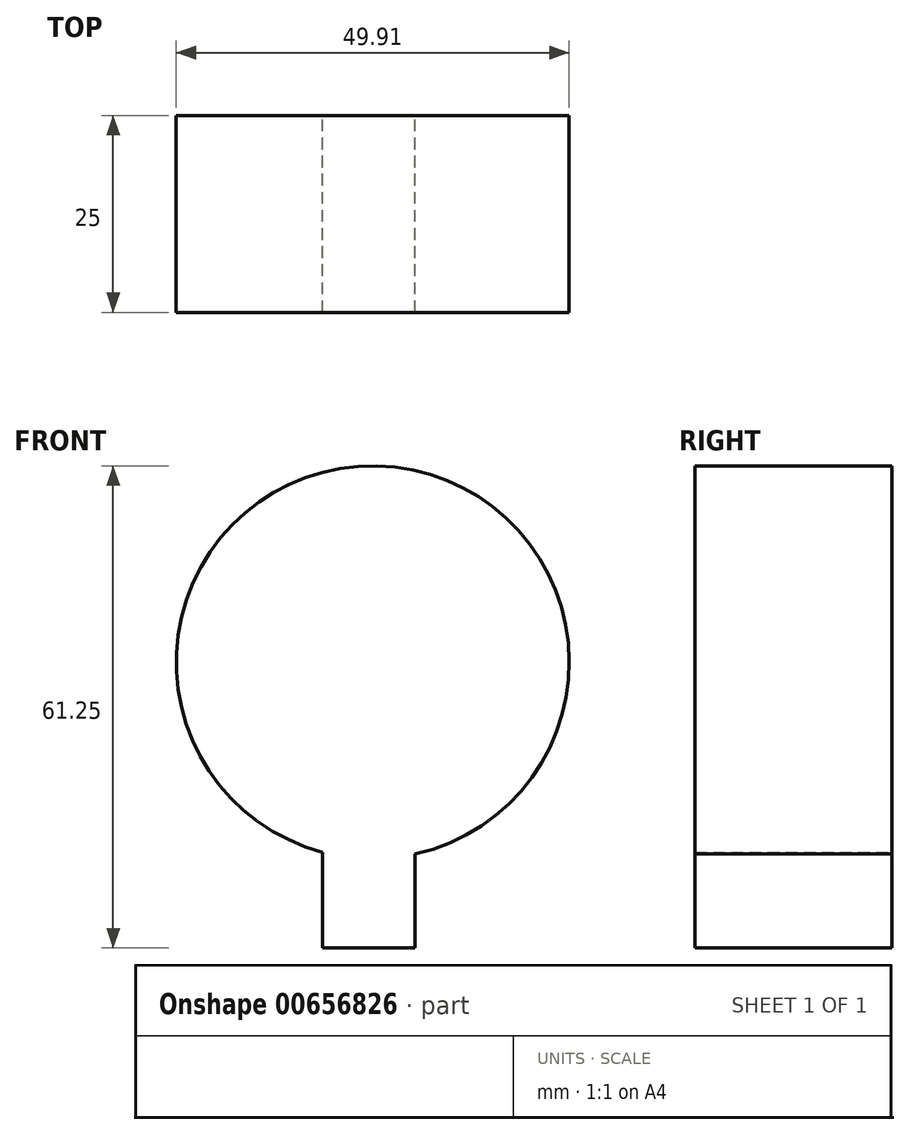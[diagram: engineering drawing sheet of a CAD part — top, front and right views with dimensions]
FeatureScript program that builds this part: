
annotation { "Feature Type Name" : "Feature", "Feature Type Description" : "" }
export const myFeature = defineFeature(function(context is Context, id is Id, definition is map)
    precondition{}
    {
        {
            var Q0;
            Q0=qCreatedBy(makeId("Front.planeOp"),FACE);
            var sketch = newSketch(context, id + "F0", { "sketchPlane" : qUnion([Q0])});
            skCircle(sketch, "E0", {"center": v(-20.84, 43.2) * mm, "radius": 24.96 * mm});
            skLineSegment(sketch, "E1", {"start": v(-27.2, 19.06) * mm, "end": v(-27.2, 6.9) * mm});
            skLineSegment(sketch, "E2", {"start": v(-15.45, 18.83) * mm, "end": v(-15.45, 6.9) * mm});
            skLineSegment(sketch, "E3", {"start": v(-27.2, 6.9) * mm, "end": v(-15.45, 6.9) * mm});
            skSolve(sketch);
        }
        {
            var Q0;
            Q0 = qSketchRegion(id + "F0", true);
            extrude(context, id + "F1", {"entities" : qUnion([Q0]), "depth" : 25 * mm, "offsetDistance" : 25 * mm});
        }
    });
